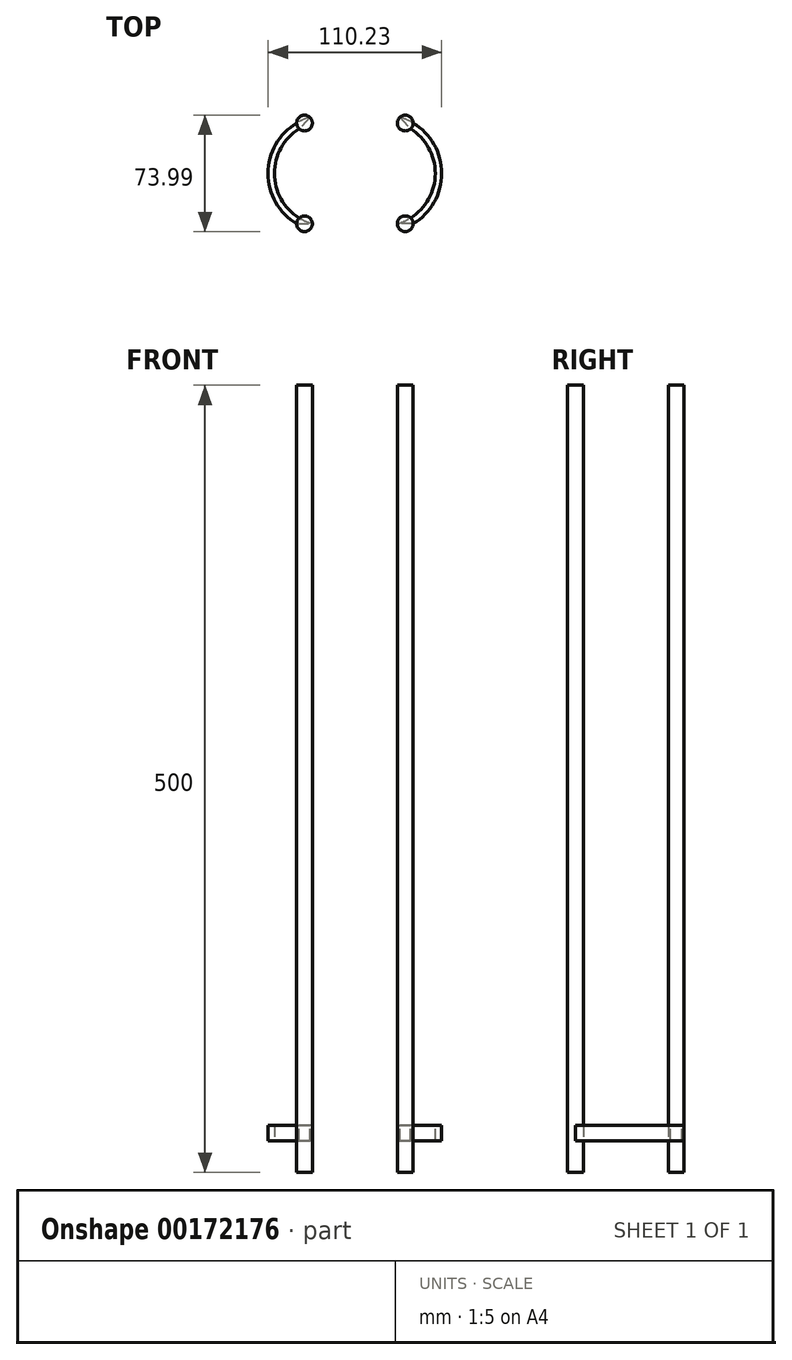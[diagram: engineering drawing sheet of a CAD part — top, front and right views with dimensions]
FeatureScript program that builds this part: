
annotation { "Feature Type Name" : "Feature", "Feature Type Description" : "" }
export const myFeature = defineFeature(function(context is Context, id is Id, definition is map)
    precondition{}
    {
        {
            var Q0;
            Q0=qCreatedBy(makeId("Top.planeOp"),FACE);
            var sketch = newSketch(context, id + "F0", { "sketchPlane" : qUnion([Q0])});
            skCircle(sketch, "E0", {"center": v(0, 0) * mm, "radius": 40 * mm});
            skSolve(sketch);
        }
        {
            var Q0;
            Q0=qCreatedBy(makeId("Top.planeOp"),FACE);
            var sketch = newSketch(context, id + "F1", { "sketchPlane" : qUnion([Q0])});
            skCircle(sketch, "E1", {"center": v(-31.82, -31.82) * mm, "radius": 5 * mm});
            skCircle(sketch, "E2.1.0", {"center": v(-31.82, 32.17) * mm, "radius": 5 * mm});
            skCircle(sketch, "E2.2.0", {"center": v(32.17, 32.17) * mm, "radius": 5 * mm});
            skCircle(sketch, "E2.3.0", {"center": v(32.17, -31.82) * mm, "radius": 5 * mm});
            skPoint(sketch, "E2.center", {"position": v(0.18, 0.18) * mm});
            skLineSegment(sketch, "E2.anchor1", {"start": v(0.18, 0.18) * mm, "end": v(-31.82, -31.82) * mm, "construction": true});
            skLineSegment(sketch, "E2.anchor2", {"start": v(0.18, 0.18) * mm, "end": v(32.17, -31.82) * mm, "construction": true});
            skSolve(sketch);
        }
        {
            var Q0;
            Q0 = qSketchRegion(id + "F1", true);
            extrude(context, id + "F2", {"entities" : qUnion([Q0]), "depth" : 500 * mm});
        }
        {
            var Q0;
            Q0=qCreatedBy(makeId("Top.planeOp"),FACE);
            cPlane(context, id + "F3", {"entities" : qUnion([Q0]), "cplaneType" : CPlaneType.OFFSET, "offset" : 25 * mm, "width" : 150 * mm, "height" : 150 * mm});
        }
        {
            var Q0;
            Q0=qCreatedBy(id+"F3.planeOp",FACE);
            var sketch = newSketch(context, id + "F4", { "sketchPlane" : qUnion([Q0])});
            skArc(sketch, "E3", {"start": v(-31.82, 32.17) * mm, "mid": v(-52.63, 0.18) * mm, "end": v(-31.82, -31.82) * mm});
            skArc(sketch, "E4", {"start": v(32.17, -31.82) * mm, "mid": v(52.99, 0.18) * mm, "end": v(32.17, 32.17) * mm});
            skSolve(sketch);
        }
        {
            var Q0;
            Q0=qCreatedBy(makeId("Front.planeOp"),FACE);
            var Q1;
            Q1=sQuery(id+"F4.wireOp",VERTEX,"E3.end");
            cPlane(context, id + "F5", {"entities" : qUnion([Q0, Q1]), "cplaneType" : CPlaneType.PLANE_POINT, "offset" : 35 * mm, "width" : 150 * mm, "height" : 150 * mm});
        }
        {
            var Q0;
            Q0=qCreatedBy(id+"F5.planeOp",FACE);
            var sketch = newSketch(context, id + "F6", { "sketchPlane" : qUnion([Q0])});
            skLineSegment(sketch, "E5.bottom", {"start": v(-36.82, 20) * mm, "end": v(-26.82, 20) * mm});
            skLineSegment(sketch, "E5.top", {"start": v(-36.82, 30) * mm, "end": v(-26.82, 30) * mm});
            skLineSegment(sketch, "E5.left", {"start": v(-36.82, 20) * mm, "end": v(-36.82, 30) * mm});
            skLineSegment(sketch, "E5.right", {"start": v(-26.82, 20) * mm, "end": v(-26.82, 30) * mm});
            skPoint(sketch, "E5.middle", {"position": v(-31.82, 25) * mm});
            skSolve(sketch);
        }
        {
            var Q0;
            Q0 = qSketchRegion(id + "F6", true);
            var Q1;
            Q1=sQuery(id+"F4.wireOp",EDGE,"E3");
            sweep(context, id + "F7", {"profiles" : qUnion([Q0]), "path" : qUnion([Q1])});
        }
        {
            var Q0;
            Q0=qCreatedBy(id+"F5.planeOp",FACE);
            var sketch = newSketch(context, id + "F8", { "sketchPlane" : qUnion([Q0])});
            skLineSegment(sketch, "E6.bottom", {"start": v(37.17, 20) * mm, "end": v(27.17, 20) * mm});
            skLineSegment(sketch, "E6.top", {"start": v(37.17, 30) * mm, "end": v(27.17, 30) * mm});
            skLineSegment(sketch, "E6.left", {"start": v(37.17, 20) * mm, "end": v(37.17, 30) * mm});
            skLineSegment(sketch, "E6.right", {"start": v(27.17, 20) * mm, "end": v(27.17, 30) * mm});
            skPoint(sketch, "E6.middle", {"position": v(32.17, 25) * mm});
            skSolve(sketch);
        }
        {
            var Q0;
            Q0 = qSketchRegion(id + "F8", true);
            var Q1;
            Q1=sQuery(id+"F4.wireOp",EDGE,"E4");
            sweep(context, id + "F9", {"profiles" : qUnion([Q0]), "path" : qUnion([Q1])});
        }
    });
